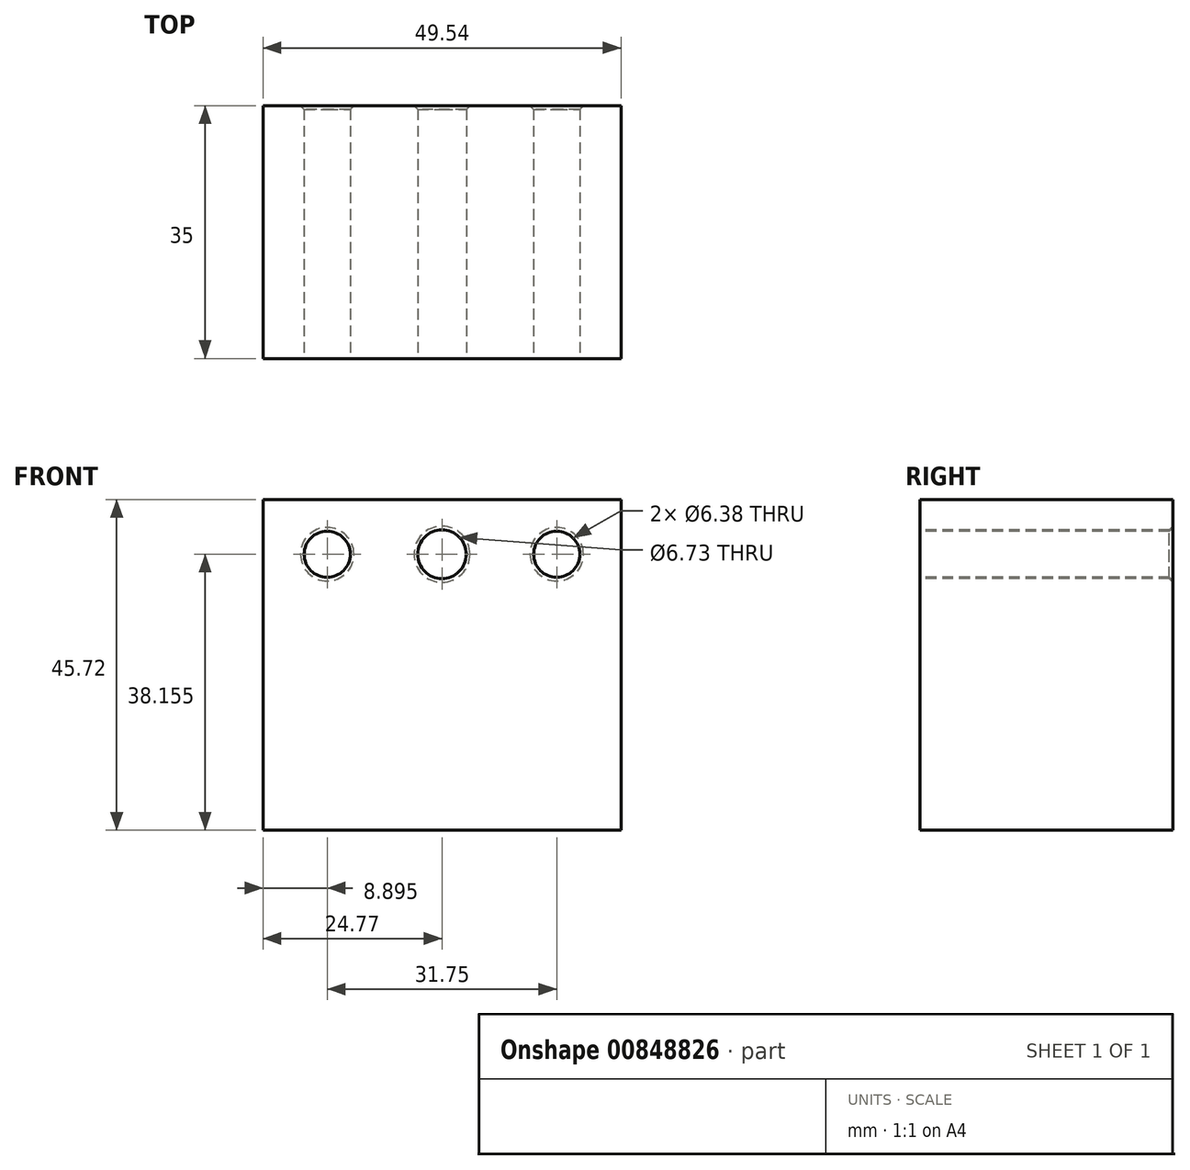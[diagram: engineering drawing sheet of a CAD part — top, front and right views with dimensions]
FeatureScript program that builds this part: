
annotation { "Feature Type Name" : "Feature", "Feature Type Description" : "" }
export const myFeature = defineFeature(function(context is Context, id is Id, definition is map)
    precondition{}
    {
        {
            var Q0;
            Q0=qCreatedBy(makeId("Front.planeOp"),FACE);
            var sketch = newSketch(context, id + "F0", { "sketchPlane" : qUnion([Q0])});
            skLineSegment(sketch, "E0.bottom", {"start": v(-24.77, -26.38) * mm, "end": v(24.77, -26.38) * mm});
            skLineSegment(sketch, "E0.top", {"start": v(-24.77, 19.34) * mm, "end": v(24.77, 19.34) * mm});
            skLineSegment(sketch, "E0.left", {"start": v(-24.77, -26.38) * mm, "end": v(-24.77, 19.34) * mm});
            skLineSegment(sketch, "E0.right", {"start": v(24.77, -26.38) * mm, "end": v(24.77, 19.34) * mm});
            skPoint(sketch, "E1", {"position": v(-15.88, 11.78) * mm});
            skPoint(sketch, "E2", {"position": v(0, 11.78) * mm});
            skPoint(sketch, "E3", {"position": v(15.88, 11.78) * mm});
            skSolve(sketch);
        }
        {
            var Q0;
            Q0=makeQuery(id+"F0.imprint","IMPRINT",FACE,{"disambiguationData":[TD([[makeQuery(id+"F0.imprint","IMPRINT",EDGE,{"derivedFrom":sQuery(id+"F0.wireOp",EDGE,"E0.bottom")}),1.0]])]});
            extrude(context, id + "F1", {"entities" : qUnion([Q0]), "depth" : 35 * mm, "offsetDistance" : 25.4 * mm});
        }
        {
            var Q0;
            Q0=makeQuery(id+"F1.opExtrude","CAP_FACE",FACE,{"disambiguationData":[OSD([sQuery(id+"F0.wireOp",EDGE,"E0.bottom"),sQuery(id+"F0.wireOp",EDGE,"E0.top"),sQuery(id+"F0.wireOp",EDGE,"E0.left"),sQuery(id+"F0.wireOp",EDGE,"E0.right")])],"isStart":false});
            var sketch = newSketch(context, id + "F2", { "sketchPlane" : qUnion([Q0])});
            skSolve(sketch);
        }
        {
            var Q0;
            Q0=makeQuery(id+"F2.imprint","IMPRINT",FACE,{"disambiguationData":[TD([[makeQuery(id+"F2.imprint","IMPRINT",EDGE,{"derivedFrom":makeQuery(id+"F1.opExtrude","CAP_EDGE",EDGE,{"disambiguationData":[OSD([sQuery(id+"F0.wireOp",EDGE,"E0.bottom")])],"isStart":false})}),1.0]])]});
            var sketch = newSketch(context, id + "F3", { "sketchPlane" : qUnion([Q0])});
            skCircle(sketch, "E4", {"center": v(0, 11.78) * mm, "radius": 3.37 * mm});
            skCircle(sketch, "E5", {"center": v(15.88, 11.78) * mm, "radius": 3.19 * mm});
            skCircle(sketch, "E6", {"center": v(-15.88, 11.78) * mm, "radius": 3.19 * mm});
            skSolve(sketch);
        }
        {
            var Q0;
            Q0=makeQuery(id+"F3.imprint","IMPRINT",FACE,{"disambiguationData":[TD([[makeQuery(id+"F3.imprint","IMPRINT",EDGE,{"derivedFrom":sQuery(id+"F3.wireOp",EDGE,"E6")}),1.0]])]});
            var Q1;
            Q1=makeQuery(id+"F3.imprint","IMPRINT",FACE,{"disambiguationData":[TD([[makeQuery(id+"F3.imprint","IMPRINT",EDGE,{"derivedFrom":sQuery(id+"F3.wireOp",EDGE,"E5")}),1.0]])]});
            extrude(context, id + "F4", {"entities" : qUnion([Q0, Q1]), "operationType" : NewBodyOperationType.REMOVE, "endBound" : BoundingType.THROUGH_ALL, "oppositeDirection" : true, "depth" : 12.7 * mm, "offsetDistance" : 25.4 * mm});
        }
        {
            var Q0;
            Q0=makeQuery(id+"F3.imprint","IMPRINT",FACE,{"disambiguationData":[TD([[makeQuery(id+"F3.imprint","IMPRINT",EDGE,{"derivedFrom":sQuery(id+"F3.wireOp",EDGE,"E4")}),1.0]])]});
            extrude(context, id + "F5", {"entities" : qUnion([Q0]), "operationType" : NewBodyOperationType.REMOVE, "endBound" : BoundingType.THROUGH_ALL, "oppositeDirection" : true, "depth" : 25.4 * mm, "offsetDistance" : 25.4 * mm});
        }
        {
            var Q0;
            Q0=makeQuery(id+"F5.boolean.opBoolean","INTERSECT",EDGE,{"derivedFrom":[makeQuery(id+"F1.opExtrude","CAP_FACE",FACE,{"disambiguationData":[OSD([sQuery(id+"F0.wireOp",EDGE,"E0.bottom"),sQuery(id+"F0.wireOp",EDGE,"E0.top"),sQuery(id+"F0.wireOp",EDGE,"E0.left"),sQuery(id+"F0.wireOp",EDGE,"E0.right")])],"isStart":true}),makeQuery(id+"F5.opExtrude","SWEPT_FACE",FACE,{"disambiguationData":[OSD([sQuery(id+"F3.wireOp",EDGE,"E4")])]})]});
            var Q1;
            Q1=makeQuery(id+"F4.boolean.opBoolean","COPY",EDGE,{"derivedFrom":makeQuery(id+"F4.opExtrude","CAP_EDGE",EDGE,{"disambiguationData":[OSD([sQuery(id+"F3.wireOp",EDGE,"E5")])],"isStart":true})});
            var Q2;
            Q2=makeQuery(id+"F5.boolean.opBoolean","COPY",EDGE,{"derivedFrom":makeQuery(id+"F5.opExtrude","CAP_EDGE",EDGE,{"disambiguationData":[OSD([sQuery(id+"F3.wireOp",EDGE,"E4")])],"isStart":true})});
            var Q3;
            Q3=makeQuery(id+"F4.boolean.opBoolean","COPY",EDGE,{"derivedFrom":makeQuery(id+"F4.opExtrude","CAP_EDGE",EDGE,{"disambiguationData":[OSD([sQuery(id+"F3.wireOp",EDGE,"E6")])],"isStart":true})});
            var Q4;
            Q4=makeQuery(id+"F4.boolean.opBoolean","INTERSECT",EDGE,{"derivedFrom":[makeQuery(id+"F1.opExtrude","CAP_FACE",FACE,{"disambiguationData":[OSD([sQuery(id+"F0.wireOp",EDGE,"E0.bottom"),sQuery(id+"F0.wireOp",EDGE,"E0.top"),sQuery(id+"F0.wireOp",EDGE,"E0.left"),sQuery(id+"F0.wireOp",EDGE,"E0.right")])],"isStart":true}),makeQuery(id+"F4.opExtrude","SWEPT_FACE",FACE,{"disambiguationData":[OSD([sQuery(id+"F3.wireOp",EDGE,"E5")])]})]});
            var Q5;
            Q5=makeQuery(id+"F4.boolean.opBoolean","INTERSECT",EDGE,{"derivedFrom":[makeQuery(id+"F1.opExtrude","CAP_FACE",FACE,{"disambiguationData":[OSD([sQuery(id+"F0.wireOp",EDGE,"E0.bottom"),sQuery(id+"F0.wireOp",EDGE,"E0.top"),sQuery(id+"F0.wireOp",EDGE,"E0.left"),sQuery(id+"F0.wireOp",EDGE,"E0.right")])],"isStart":true}),makeQuery(id+"F4.opExtrude","SWEPT_FACE",FACE,{"disambiguationData":[OSD([sQuery(id+"F3.wireOp",EDGE,"E6")])]})]});
            chamfer(context, id + "F6", {"entities" : qUnion([Q0, Q1, Q2, Q3, Q4, Q5]), "width" : 0.5 * mm, "tangentPropagation" : true});
        }
    });
